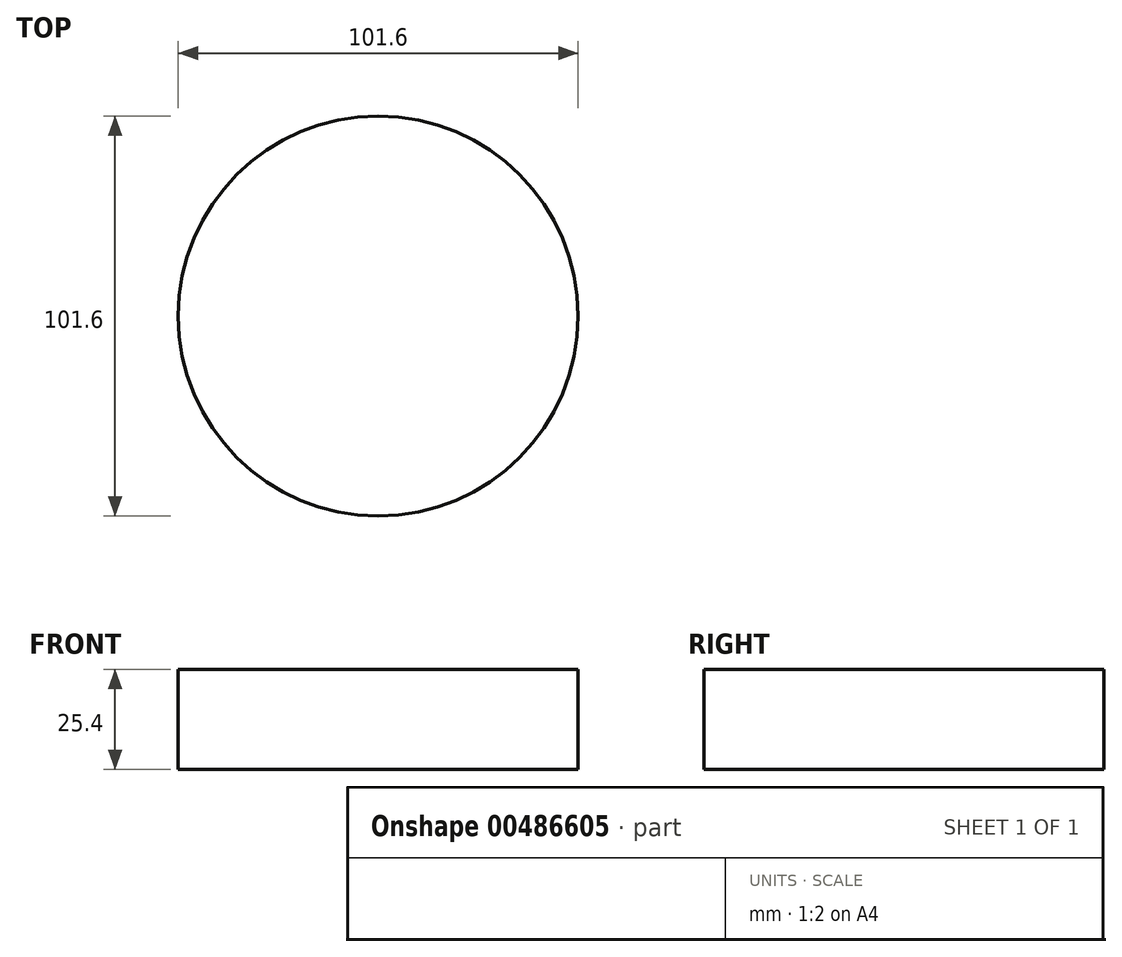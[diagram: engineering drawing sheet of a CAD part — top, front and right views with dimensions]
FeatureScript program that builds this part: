
annotation { "Feature Type Name" : "Feature", "Feature Type Description" : "" }
export const myFeature = defineFeature(function(context is Context, id is Id, definition is map)
    precondition{}
    {
        {
            var Q0;
            Q0=qCreatedBy(makeId("Top.planeOp"),FACE);
            var sketch = newSketch(context, id + "F0", { "sketchPlane" : qUnion([Q0])});
            skCircle(sketch, "E0", {"center": v(0, 0.3) * mm, "radius": 50.8 * mm});
            skSolve(sketch);
        }
        {
            var Q0;
            Q0=makeQuery(id+"F0.imprint","IMPRINT",FACE,{"disambiguationData":[TD([[makeQuery(id+"F0.imprint","IMPRINT",EDGE,{"derivedFrom":sQuery(id+"F0.wireOp",EDGE,"E0")}),1.0]])]});
            extrude(context, id + "F1", {"entities" : qUnion([Q0]), "depth" : 25.4 * mm});
        }
    });
